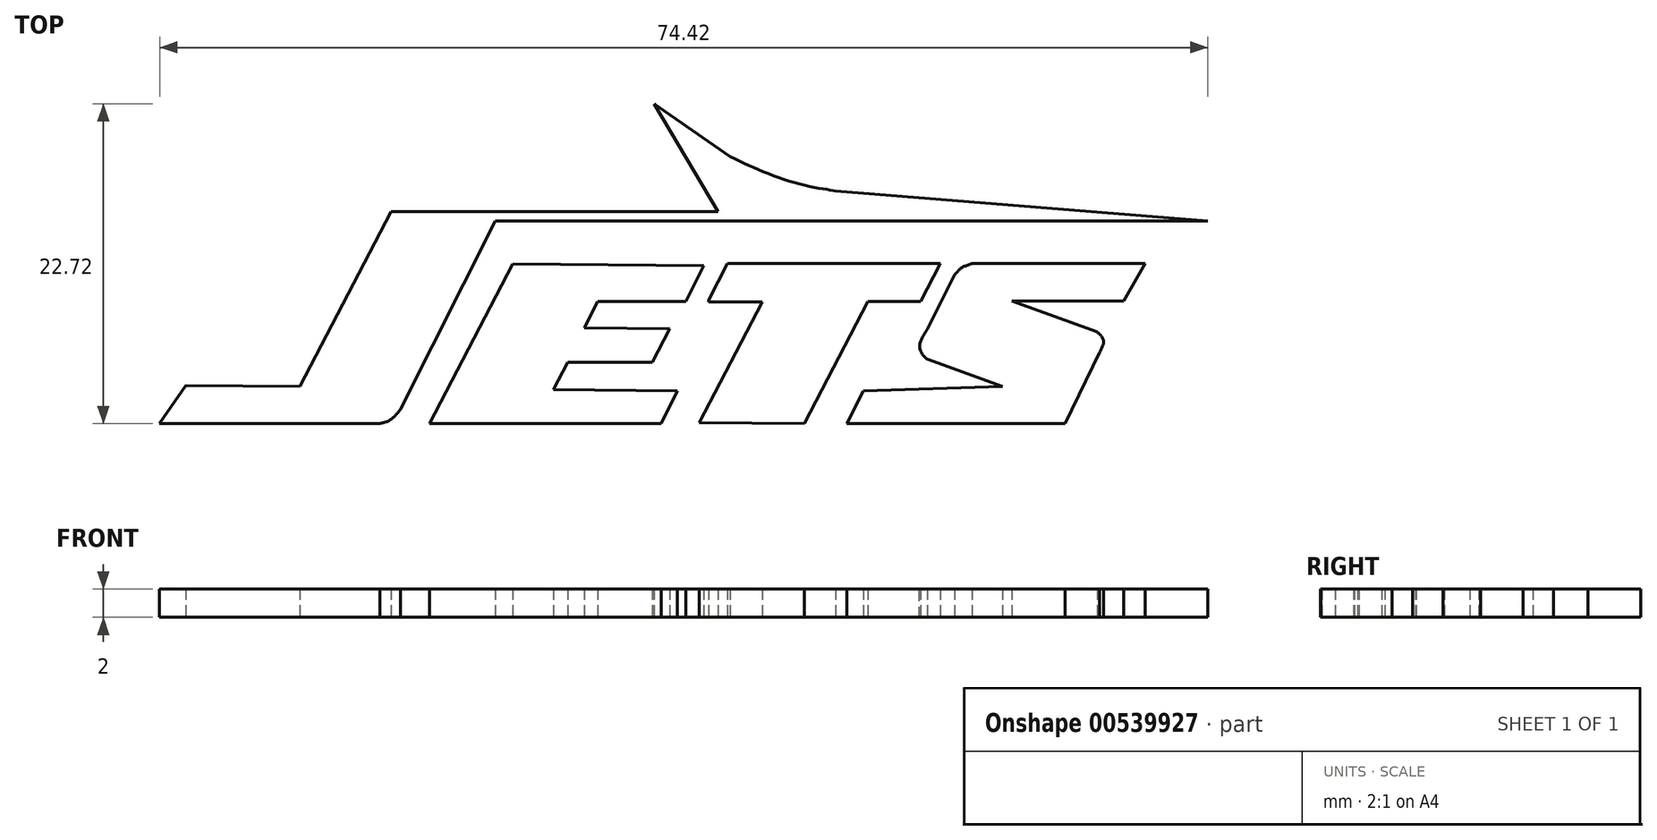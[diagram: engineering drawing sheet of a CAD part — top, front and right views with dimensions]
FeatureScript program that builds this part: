
annotation { "Feature Type Name" : "Feature", "Feature Type Description" : "" }
export const myFeature = defineFeature(function(context is Context, id is Id, definition is map)
    precondition{}
    {
        {
            var Q0;
            Q0=qCreatedBy(makeId("Top.planeOp"),FACE);
            var sketch = newSketch(context, id + "F0", { "sketchPlane" : qUnion([Q0])});
            skLineSegment(sketch, "E0", {"start": v(1.86, 2.89) * mm, "end": v(0, 0.18) * mm});
            skLineSegment(sketch, "E1", {"start": v(0, 0.18) * mm, "end": v(15.66, 0.2) * mm});
            skFitSpline(sketch, "E2", {"points": [v(15.66, 0.2) * mm, v(16.14, 0.33) * mm, v(16.62, 0.64) * mm, v(17.12, 1.2) * mm], "startDerivative": vector(1.6, 0.33) * mm, "endDerivative": vector(1.32, 1.62) * mm});
            skLineSegment(sketch, "E3", {"start": v(17.12, 1.2) * mm, "end": v(23.83, 14.56) * mm});
            skLineSegment(sketch, "E4", {"start": v(23.83, 14.56) * mm, "end": v(74.43, 14.56) * mm});
            skLineSegment(sketch, "E5", {"start": v(74.43, 14.56) * mm, "end": v(48, 16.7) * mm});
            skFitSpline(sketch, "E6", {"points": [v(48, 16.7) * mm, v(47.38, 16.8) * mm, v(46.05, 17.05) * mm, v(44.12, 17.6) * mm, v(42.2, 18.35) * mm, v(40.52, 19.14) * mm], "startDerivative": vector(-4.41, 0.73) * mm, "endDerivative": vector(-7.44, 3.6) * mm});
            skLineSegment(sketch, "E7", {"start": v(40.52, 19.14) * mm, "end": v(35.1, 22.9) * mm});
            skLineSegment(sketch, "E8", {"start": v(35.1, 22.9) * mm, "end": v(39.63, 15.25) * mm});
            skLineSegment(sketch, "E9", {"start": v(39.63, 15.25) * mm, "end": v(16.43, 15.25) * mm});
            skLineSegment(sketch, "E10", {"start": v(16.43, 15.25) * mm, "end": v(9.95, 2.82) * mm});
            skLineSegment(sketch, "E11", {"start": v(9.95, 2.82) * mm, "end": v(1.86, 2.89) * mm});
            skLineSegment(sketch, "E12", {"start": v(19.18, 0.2) * mm, "end": v(25.08, 11.52) * mm});
            skLineSegment(sketch, "E13", {"start": v(25.08, 11.52) * mm, "end": v(38.63, 11.4) * mm});
            skLineSegment(sketch, "E14", {"start": v(38.63, 11.4) * mm, "end": v(37.36, 8.86) * mm});
            skLineSegment(sketch, "E15", {"start": v(37.36, 8.86) * mm, "end": v(31.12, 8.86) * mm});
            skLineSegment(sketch, "E16", {"start": v(31.12, 8.86) * mm, "end": v(30.17, 6.97) * mm});
            skLineSegment(sketch, "E17", {"start": v(30.17, 6.97) * mm, "end": v(36.23, 6.92) * mm});
            skLineSegment(sketch, "E18", {"start": v(36.23, 6.92) * mm, "end": v(34.98, 4.52) * mm});
            skLineSegment(sketch, "E19", {"start": v(34.98, 4.52) * mm, "end": v(28.99, 4.52) * mm});
            skLineSegment(sketch, "E20", {"start": v(28.99, 4.52) * mm, "end": v(27.98, 2.59) * mm});
            skLineSegment(sketch, "E21", {"start": v(27.98, 2.59) * mm, "end": v(36.77, 2.51) * mm});
            skLineSegment(sketch, "E22", {"start": v(36.77, 2.51) * mm, "end": v(35.6, 0.2) * mm});
            skLineSegment(sketch, "E23", {"start": v(35.6, 0.2) * mm, "end": v(19.18, 0.2) * mm});
            skLineSegment(sketch, "E24", {"start": v(38.97, 8.95) * mm, "end": v(40.32, 11.55) * mm});
            skLineSegment(sketch, "E25", {"start": v(40.32, 11.55) * mm, "end": v(55.43, 11.55) * mm});
            skLineSegment(sketch, "E26", {"start": v(55.43, 11.55) * mm, "end": v(54.03, 8.86) * mm});
            skLineSegment(sketch, "E27", {"start": v(54.03, 8.86) * mm, "end": v(50.3, 8.86) * mm});
            skLineSegment(sketch, "E28", {"start": v(50.3, 8.86) * mm, "end": v(45.79, 0.2) * mm});
            skLineSegment(sketch, "E29", {"start": v(45.79, 0.2) * mm, "end": v(38.33, 0.26) * mm});
            skLineSegment(sketch, "E30", {"start": v(38.33, 0.26) * mm, "end": v(42.8, 8.83) * mm});
            skLineSegment(sketch, "E31", {"start": v(42.8, 8.83) * mm, "end": v(38.97, 8.83) * mm});
            skLineSegment(sketch, "E32", {"start": v(38.97, 8.83) * mm, "end": v(38.97, 8.95) * mm});
            skLineSegment(sketch, "E33", {"start": v(48.8, 0.2) * mm, "end": v(49.96, 2.51) * mm});
            skLineSegment(sketch, "E34", {"start": v(49.96, 2.51) * mm, "end": v(59.86, 2.82) * mm});
            skLineSegment(sketch, "E35", {"start": v(59.86, 2.82) * mm, "end": v(54.52, 4.75) * mm});
            skFitSpline(sketch, "E36", {"points": [v(54.52, 4.75) * mm, v(54.21, 5.03) * mm, v(53.96, 5.56) * mm, v(54.1, 6.17) * mm, v(54.52, 6.9) * mm], "startDerivative": vector(-1.5, 1.2) * mm, "endDerivative": vector(1.59, 2.48) * mm});
            skLineSegment(sketch, "E37", {"start": v(54.52, 6.9) * mm, "end": v(56.44, 10.76) * mm});
            skFitSpline(sketch, "E38", {"points": [v(56.44, 10.76) * mm, v(56.65, 10.97) * mm, v(56.93, 11.25) * mm, v(57.43, 11.45) * mm, v(57.68, 11.55) * mm], "startDerivative": vector(0.9, 0.9) * mm, "endDerivative": vector(1.01, 0.43) * mm});
            skLineSegment(sketch, "E39", {"start": v(57.68, 11.55) * mm, "end": v(69.98, 11.55) * mm});
            skLineSegment(sketch, "E40", {"start": v(69.98, 11.55) * mm, "end": v(68.44, 8.87) * mm});
            skLineSegment(sketch, "E41", {"start": v(68.44, 8.87) * mm, "end": v(60.51, 8.87) * mm});
            skLineSegment(sketch, "E42", {"start": v(60.51, 8.87) * mm, "end": v(66.56, 6.7) * mm});
            skFitSpline(sketch, "E43", {"points": [v(66.56, 6.7) * mm, v(66.9, 6.34) * mm, v(67.02, 5.94) * mm, v(66.97, 5.74) * mm, v(66.75, 5.25) * mm], "startDerivative": vector(1.4, -1.18) * mm, "endDerivative": vector(-0.86, -1.91) * mm});
            skLineSegment(sketch, "E44", {"start": v(66.75, 5.25) * mm, "end": v(64.3, 0.2) * mm});
            skLineSegment(sketch, "E45", {"start": v(64.3, 0.2) * mm, "end": v(48.8, 0.2) * mm});
            skSolve(sketch);
        }
        {
            var Q0;
            Q0 = qSketchRegion(id + "F0", true);
            extrude(context, id + "F1", {"entities" : qUnion([Q0]), "depth" : 2 * mm, "offsetDistance" : 25.4 * mm});
        }
    });
